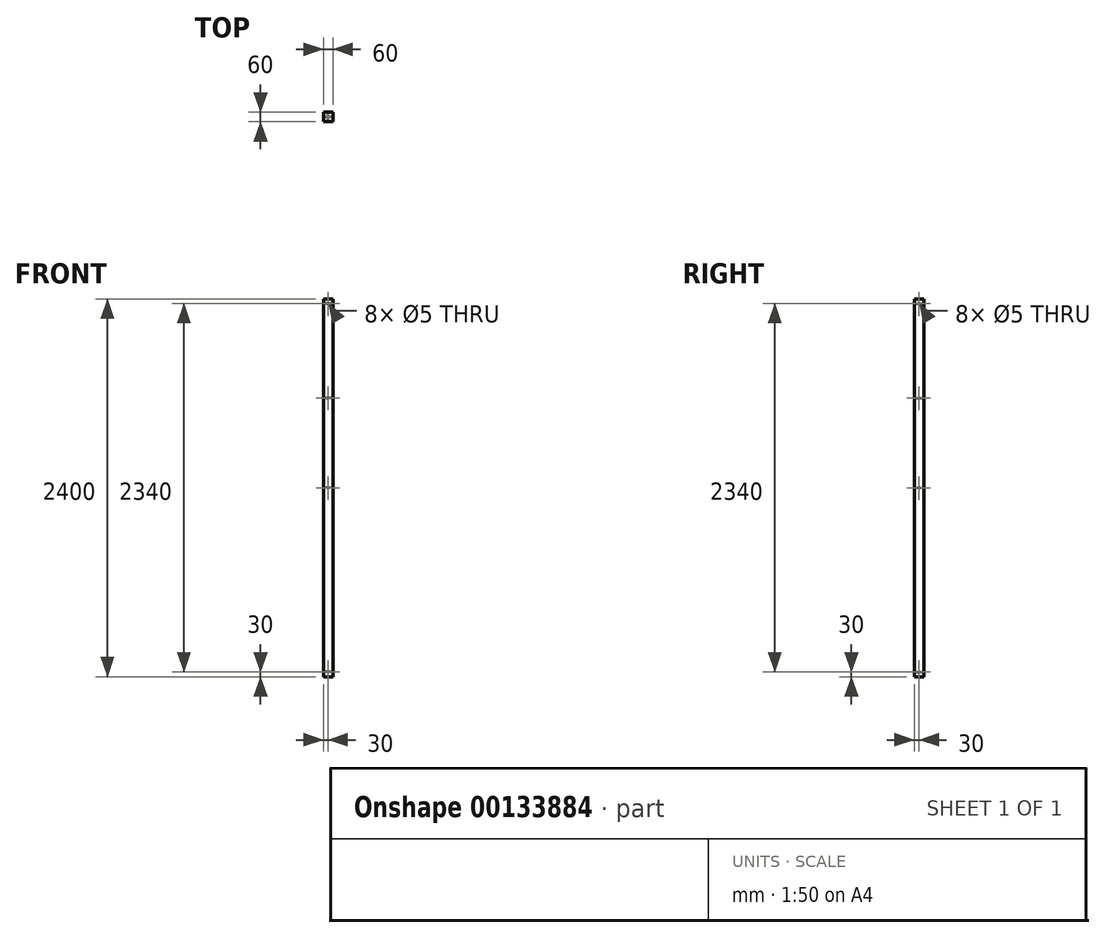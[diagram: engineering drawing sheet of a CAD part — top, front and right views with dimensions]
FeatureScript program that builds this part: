
annotation { "Feature Type Name" : "Feature", "Feature Type Description" : "" }
export const myFeature = defineFeature(function(context is Context, id is Id, definition is map)
    precondition{}
    {
        {
            assignVariable(context, id + "F0", {"name" : "Laenge", "anyValue" : 2400 * mm});
        }
        {
            var Q0;
            Q0=qCreatedBy(makeId("Top.planeOp"),FACE);
            var sketch = newSketch(context, id + "F1", { "sketchPlane" : qUnion([Q0])});
            skLineSegment(sketch, "E0.bottom", {"start": v(-30, 30) * mm, "end": v(30, 30) * mm});
            skLineSegment(sketch, "E0.top", {"start": v(-30, -30) * mm, "end": v(30, -30) * mm});
            skLineSegment(sketch, "E0.left", {"start": v(-30, 30) * mm, "end": v(-30, -30) * mm});
            skLineSegment(sketch, "E0.right", {"start": v(30, 30) * mm, "end": v(30, -30) * mm});
            skPoint(sketch, "E1", {"position": v(0, 30) * mm});
            skPoint(sketch, "E2", {"position": v(30, 0) * mm});
            skLineSegment(sketch, "E3", {"start": v(0, 30) * mm, "end": v(0, 0) * mm, "construction": true});
            skLineSegment(sketch, "E4", {"start": v(0, 0) * mm, "end": v(30, 0) * mm, "construction": true});
            skSolve(sketch);
        }
        {
            var Q0;
            Q0 = qSketchRegion(id + "F1", true);
            extrude(context, id + "F2", {"entities" : qUnion([Q0]), "depth" : getVariable(context, 'Laenge')});
        }
        {
            var Q0;
            Q0=makeQuery(id+"F2.opExtrude","SWEPT_FACE",FACE,{"disambiguationData":[OSD([sQuery(id+"F1.wireOp",EDGE,"E0.left")])]});
            var sketch = newSketch(context, id + "F3", { "sketchPlane" : qUnion([Q0])});
            skPoint(sketch, "E5", {"position": v(0, 1200) * mm});
            skLineSegment(sketch, "E6", {"start": v(-30, 1200) * mm, "end": v(30, 1200) * mm, "construction": true});
            skPoint(sketch, "E7", {"position": v(0, 30) * mm});
            skPoint(sketch, "E8.MirrorP", {"position": v(0, 2370) * mm});
            skPoint(sketch, "E9", {"position": v(0, 1770) * mm});
            skSolve(sketch);
        }
        {
            var Q0;
            Q0=makeQuery(id+"F2.opExtrude","SWEPT_FACE",FACE,{"disambiguationData":[OSD([sQuery(id+"F1.wireOp",EDGE,"E0.bottom")])]});
            var sketch = newSketch(context, id + "F4", { "sketchPlane" : qUnion([Q0])});
            skPoint(sketch, "E10", {"position": v(0, 1200) * mm});
            skPoint(sketch, "E11", {"position": v(0, 30) * mm});
            skLineSegment(sketch, "E12", {"start": v(-30, 1200) * mm, "end": v(30, 1200) * mm, "construction": true});
            skPoint(sketch, "E13.MirrorP", {"position": v(0, 2370) * mm});
            skPoint(sketch, "E14", {"position": v(0, 1770) * mm});
            skSolve(sketch);
        }
        {
            var Q0;
            Q0=sQuery(id+"F4.wireOp",VERTEX,"E10");
            var Q1;
            Q1=sQuery(id+"F3.wireOp",VERTEX,"E5");
            var Q2;
            Q2=sQuery(id+"F3.wireOp",VERTEX,"E7");
            var Q3;
            Q3=sQuery(id+"F4.wireOp",VERTEX,"E11");
            var Q4;
            Q4=sQuery(id+"F4.wireOp",VERTEX,"E13.MirrorP");
            var Q5;
            Q5=sQuery(id+"F3.wireOp",VERTEX,"E8.MirrorP");
            var Q6;
            Q6=sQuery(id+"F3.wireOp",VERTEX,"E9");
            var Q7;
            Q7=sQuery(id+"F4.wireOp",VERTEX,"E14");
            var Q8;
            Q8=makeQuery(id+"F2.opExtrude","SWEPT_BODY",BODY,{"disambiguationData":[OSD([sQuery(id+"F1.wireOp",EDGE,"E0.bottom"),sQuery(id+"F1.wireOp",EDGE,"E0.top"),sQuery(id+"F1.wireOp",EDGE,"E0.left"),sQuery(id+"F1.wireOp",EDGE,"E0.right")])]});
            hole(context, id + "F5", {"style" : HoleStyle.SIMPLE, "endStyle" : HoleEndStyle.THROUGH, "holeDiameter" : 5 * mm, "startFromSketch" : true, "locations" : qUnion([Q0, Q1, Q2, Q3, Q4, Q5, Q6, Q7]), "scope" : qUnion([Q8]), "isTappedThrough" : true});
        }
    });
